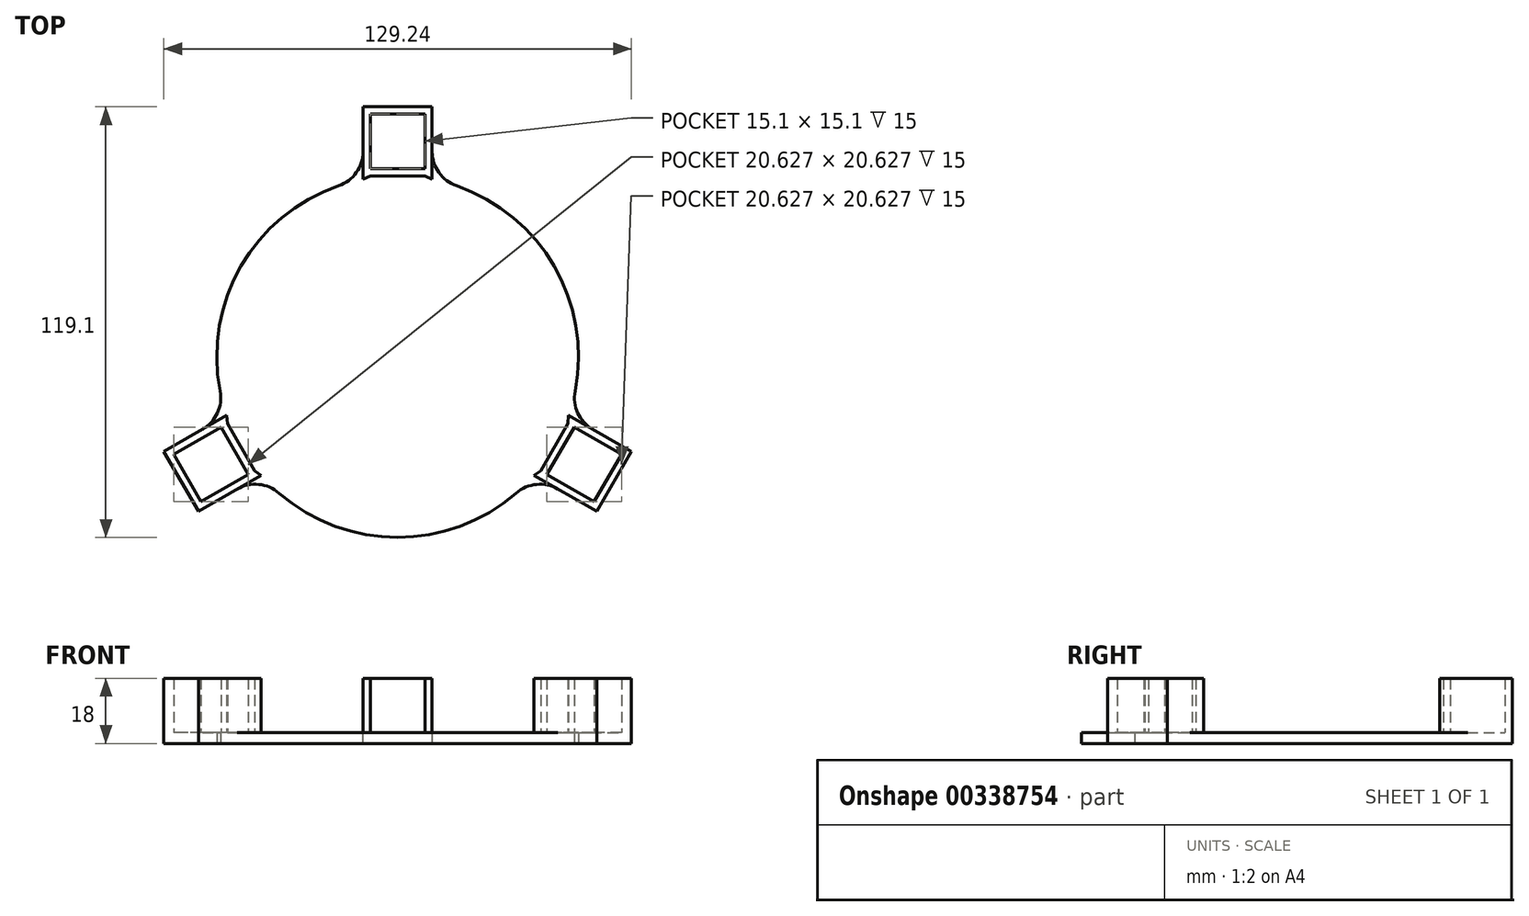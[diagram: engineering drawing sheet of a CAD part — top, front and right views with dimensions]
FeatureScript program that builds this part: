
annotation { "Feature Type Name" : "Feature", "Feature Type Description" : "" }
export const myFeature = defineFeature(function(context is Context, id is Id, definition is map)
    precondition{}
    {
        {
            var Q0;
            Q0=qCreatedBy(makeId("Top.planeOp"),FACE);
            var sketch = newSketch(context, id + "F0", { "sketchPlane" : qUnion([Q0])});
            skCircle(sketch, "E0", {"center": v(0, 0) * mm, "radius": 50 * mm});
            skSolve(sketch);
        }
        {
            var Q0;
            Q0=makeQuery(id+"F0.imprint","IMPRINT",FACE,{"disambiguationData":[TD([[makeQuery(id+"F0.imprint","IMPRINT",EDGE,{"derivedFrom":sQuery(id+"F0.wireOp",EDGE,"E0")}),1.0]])]});
            extrude(context, id + "F1", {"entities" : qUnion([Q0]), "depth" : 3 * mm});
        }
        {
            var Q0;
            Q0=qCreatedBy(makeId("Top.planeOp"),FACE);
            var sketch = newSketch(context, id + "F2", { "sketchPlane" : qUnion([Q0])});
            skLineSegment(sketch, "E1", {"start": v(0, 0) * mm, "end": v(0, 59.55) * mm, "construction": true});
            skCircle(sketch, "E2.0", {"center": v(0, 0) * mm, "radius": 50 * mm});
            skPoint(sketch, "E3", {"position": v(0, 50) * mm});
            skLineSegment(sketch, "E4.bottom", {"start": v(7.55, 50) * mm, "end": v(-7.55, 50) * mm});
            skLineSegment(sketch, "E4.top", {"start": v(7.55, 69.1) * mm, "end": v(-7.55, 69.1) * mm});
            skLineSegment(sketch, "E4.left", {"start": v(7.55, 50) * mm, "end": v(7.55, 69.1) * mm});
            skLineSegment(sketch, "E4.right", {"start": v(-7.55, 50) * mm, "end": v(-7.55, 69.1) * mm});
            skPoint(sketch, "E4.middle", {"position": v(0, 59.55) * mm});
            skLineSegment(sketch, "E5", {"start": v(-7.55, 52) * mm, "end": v(7.55, 52) * mm});
            skLineSegment(sketch, "E6", {"start": v(-7.55, 67.1) * mm, "end": v(7.55, 67.1) * mm});
            skLineSegment(sketch, "E7.bottom", {"start": v(-7.55, 69.1) * mm, "end": v(-9.55, 69.1) * mm});
            skLineSegment(sketch, "E7.top", {"start": v(-7.55, 67.1) * mm, "end": v(-9.55, 67.1) * mm});
            skLineSegment(sketch, "E7.left", {"start": v(-7.55, 69.1) * mm, "end": v(-7.55, 67.1) * mm});
            skLineSegment(sketch, "E7.right", {"start": v(-9.55, 69.1) * mm, "end": v(-9.55, 67.1) * mm});
            skLineSegment(sketch, "E8.bottom", {"start": v(7.55, 69.1) * mm, "end": v(9.55, 69.1) * mm});
            skLineSegment(sketch, "E8.top", {"start": v(7.55, 67.1) * mm, "end": v(9.55, 67.1) * mm});
            skLineSegment(sketch, "E8.left", {"start": v(7.55, 69.1) * mm, "end": v(7.55, 67.1) * mm});
            skLineSegment(sketch, "E8.right", {"start": v(9.55, 69.1) * mm, "end": v(9.55, 67.1) * mm});
            skLineSegment(sketch, "E9", {"start": v(-7.55, 50) * mm, "end": v(-9.55, 49.08) * mm});
            skLineSegment(sketch, "E10", {"start": v(7.55, 50) * mm, "end": v(9.55, 49.08) * mm});
            skLineSegment(sketch, "E11", {"start": v(-9.55, 67.1) * mm, "end": v(-9.55, 49.08) * mm});
            skLineSegment(sketch, "E12", {"start": v(9.55, 67.1) * mm, "end": v(9.55, 49.08) * mm});
            skLineSegment(sketch, "E13.1.0", {"start": v(-53.34, -41.82) * mm, "end": v(-37.73, -32.81) * mm});
            skLineSegment(sketch, "E13.1.1", {"start": v(-62.89, -25.28) * mm, "end": v(-47.28, -16.27) * mm});
            skLineSegment(sketch, "E13.1.2", {"start": v(-54.34, -40.09) * mm, "end": v(-61.89, -27.01) * mm});
            skLineSegment(sketch, "E13.1.3", {"start": v(-41.26, -32.54) * mm, "end": v(-48.8, -19.46) * mm});
            skLineSegment(sketch, "E13.1.4", {"start": v(-39.53, -31.54) * mm, "end": v(-56.07, -41.09) * mm});
            skLineSegment(sketch, "E13.1.5", {"start": v(-47.08, -18.46) * mm, "end": v(-63.62, -28.01) * mm});
            skLineSegment(sketch, "E13.1.6", {"start": v(-63.62, -28.01) * mm, "end": v(-56.07, -41.09) * mm});
            skLineSegment(sketch, "E13.1.7", {"start": v(-47.08, -18.46) * mm, "end": v(-39.53, -31.54) * mm});
            skLineSegment(sketch, "E13.1.8", {"start": v(0, 0) * mm, "end": v(-51.57, -29.77) * mm, "construction": true});
            skPoint(sketch, "E13.1.9", {"position": v(-51.57, -29.77) * mm});
            skPoint(sketch, "E13.1.10", {"position": v(-43.3, -25) * mm});
            skLineSegment(sketch, "E13.1.11", {"start": v(-47.08, -18.46) * mm, "end": v(-47.28, -16.27) * mm});
            skLineSegment(sketch, "E13.1.12", {"start": v(-39.53, -31.54) * mm, "end": v(-37.73, -32.81) * mm});
            skLineSegment(sketch, "E13.1.13", {"start": v(-54.34, -40.09) * mm, "end": v(-53.34, -41.82) * mm});
            skLineSegment(sketch, "E13.1.14", {"start": v(-56.07, -41.09) * mm, "end": v(-55.07, -42.82) * mm});
            skLineSegment(sketch, "E13.1.15", {"start": v(-56.07, -41.09) * mm, "end": v(-54.34, -40.09) * mm});
            skLineSegment(sketch, "E13.1.16", {"start": v(-63.62, -28.01) * mm, "end": v(-64.62, -26.28) * mm});
            skLineSegment(sketch, "E13.1.17", {"start": v(-55.07, -42.82) * mm, "end": v(-53.34, -41.82) * mm});
            skLineSegment(sketch, "E13.1.18", {"start": v(-64.62, -26.28) * mm, "end": v(-62.89, -25.28) * mm});
            skLineSegment(sketch, "E13.1.19", {"start": v(-63.62, -28.01) * mm, "end": v(-61.89, -27.01) * mm});
            skLineSegment(sketch, "E13.1.20", {"start": v(-61.89, -27.01) * mm, "end": v(-62.89, -25.28) * mm});
            skLineSegment(sketch, "E13.2.0", {"start": v(62.89, -25.28) * mm, "end": v(47.28, -16.27) * mm});
            skLineSegment(sketch, "E13.2.1", {"start": v(53.34, -41.82) * mm, "end": v(37.73, -32.81) * mm});
            skLineSegment(sketch, "E13.2.2", {"start": v(61.89, -27.01) * mm, "end": v(54.34, -40.09) * mm});
            skLineSegment(sketch, "E13.2.3", {"start": v(48.8, -19.46) * mm, "end": v(41.26, -32.54) * mm});
            skLineSegment(sketch, "E13.2.4", {"start": v(47.08, -18.46) * mm, "end": v(63.62, -28.01) * mm});
            skLineSegment(sketch, "E13.2.5", {"start": v(39.53, -31.54) * mm, "end": v(56.07, -41.09) * mm});
            skLineSegment(sketch, "E13.2.6", {"start": v(56.07, -41.09) * mm, "end": v(63.62, -28.01) * mm});
            skLineSegment(sketch, "E13.2.7", {"start": v(39.53, -31.54) * mm, "end": v(47.08, -18.46) * mm});
            skLineSegment(sketch, "E13.2.8", {"start": v(0, 0) * mm, "end": v(51.57, -29.78) * mm, "construction": true});
            skPoint(sketch, "E13.2.9", {"position": v(51.57, -29.78) * mm});
            skPoint(sketch, "E13.2.10", {"position": v(43.3, -25) * mm});
            skLineSegment(sketch, "E13.2.11", {"start": v(39.53, -31.54) * mm, "end": v(37.73, -32.81) * mm});
            skLineSegment(sketch, "E13.2.12", {"start": v(47.08, -18.46) * mm, "end": v(47.28, -16.27) * mm});
            skLineSegment(sketch, "E13.2.13", {"start": v(61.89, -27.01) * mm, "end": v(62.89, -25.28) * mm});
            skLineSegment(sketch, "E13.2.14", {"start": v(63.62, -28.01) * mm, "end": v(64.62, -26.28) * mm});
            skLineSegment(sketch, "E13.2.15", {"start": v(63.62, -28.01) * mm, "end": v(61.89, -27.01) * mm});
            skLineSegment(sketch, "E13.2.16", {"start": v(56.07, -41.09) * mm, "end": v(55.07, -42.82) * mm});
            skLineSegment(sketch, "E13.2.17", {"start": v(64.62, -26.28) * mm, "end": v(62.89, -25.28) * mm});
            skLineSegment(sketch, "E13.2.18", {"start": v(55.07, -42.82) * mm, "end": v(53.34, -41.82) * mm});
            skLineSegment(sketch, "E13.2.19", {"start": v(56.07, -41.09) * mm, "end": v(54.34, -40.09) * mm});
            skLineSegment(sketch, "E13.2.20", {"start": v(54.34, -40.09) * mm, "end": v(53.34, -41.82) * mm});
            skSolve(sketch);
        }
        {
            var Q0;
            {var subQ2=sQuery(id+"F2.wireOp",EDGE,"E5");Q0=makeQuery(id+"F2.imprint","IMPRINT",FACE,{"disambiguationData":[TD([[makeQuery(id+"F2.imprint","IMPRINT",EDGE,{"derivedFrom":subQ2}),1.0]])]});}
            var Q1;
            {var subQ0=sQuery(id+"F2.wireOp",EDGE,"E9");Q1=makeQuery(id+"F2.imprint","IMPRINT",FACE,{"disambiguationData":[TD([[makeQuery(id+"F2.imprint","IMPRINT",EDGE,{"derivedFrom":subQ0}),1.0]])]});}
            var Q2;
            {var subQ0=sQuery(id+"F2.wireOp",EDGE,"E10");Q2=makeQuery(id+"F2.imprint","IMPRINT",FACE,{"disambiguationData":[TD([[makeQuery(id+"F2.imprint","IMPRINT",EDGE,{"derivedFrom":subQ0}),-1.0]])]});}
            var Q3;
            {var subQ0=sQuery(id+"F2.wireOp",EDGE,"E13.2.2");Q3=makeQuery(id+"F2.imprint","IMPRINT",FACE,{"disambiguationData":[TD([[makeQuery(id+"F2.imprint","IMPRINT",EDGE,{"derivedFrom":subQ0}),-1.0]])]});}
            var Q4;
            {var subQ0=sQuery(id+"F2.wireOp",EDGE,"E13.2.12");Q4=makeQuery(id+"F2.imprint","IMPRINT",FACE,{"disambiguationData":[TD([[makeQuery(id+"F2.imprint","IMPRINT",EDGE,{"derivedFrom":subQ0}),1.0]])]});}
            var Q5;
            {var subQ0=sQuery(id+"F2.wireOp",EDGE,"E13.2.11");Q5=makeQuery(id+"F2.imprint","IMPRINT",FACE,{"disambiguationData":[TD([[makeQuery(id+"F2.imprint","IMPRINT",EDGE,{"derivedFrom":subQ0}),-1.0]])]});}
            var Q6;
            {var subQ0=sQuery(id+"F2.wireOp",EDGE,"E13.1.11");Q6=makeQuery(id+"F2.imprint","IMPRINT",FACE,{"disambiguationData":[TD([[makeQuery(id+"F2.imprint","IMPRINT",EDGE,{"derivedFrom":subQ0}),-1.0]])]});}
            var Q7;
            {var subQ0=sQuery(id+"F2.wireOp",EDGE,"E13.1.12");Q7=makeQuery(id+"F2.imprint","IMPRINT",FACE,{"disambiguationData":[TD([[makeQuery(id+"F2.imprint","IMPRINT",EDGE,{"derivedFrom":subQ0}),1.0]])]});}
            var Q8;
            {var subQ0=sQuery(id+"F2.wireOp",EDGE,"E13.1.2");Q8=makeQuery(id+"F2.imprint","IMPRINT",FACE,{"disambiguationData":[TD([[makeQuery(id+"F2.imprint","IMPRINT",EDGE,{"derivedFrom":subQ0}),-1.0]])]});}
            extrude(context, id + "F3", {"entities" : qUnion([Q0, Q1, Q2, Q3, Q4, Q5, Q6, Q7, Q8]), "operationType" : NewBodyOperationType.ADD, "depth" : 3 * mm});
        }
        {
            var Q0;
            Q0=makeQuery(id+"F2.imprint","IMPRINT",FACE,{"disambiguationData":[TD([[makeQuery(id+"F2.imprint","IMPRINT",EDGE,{"derivedFrom":sQuery(id+"F2.wireOp",EDGE,"E13.1.1")}),-1.0]])]});
            var Q1;
            {var subQ1=sQuery(id+"F2.wireOp",EDGE,"E13.1.3");Q1=makeQuery(id+"F2.imprint","IMPRINT",FACE,{"disambiguationData":[TD([[makeQuery(id+"F2.imprint","IMPRINT",EDGE,{"derivedFrom":subQ1}),-1.0]])]});}
            var Q2;
            Q2=makeQuery(id+"F2.imprint","IMPRINT",FACE,{"disambiguationData":[TD([[makeQuery(id+"F2.imprint","IMPRINT",EDGE,{"derivedFrom":sQuery(id+"F2.wireOp",EDGE,"E13.1.0")}),1.0]])]});
            var Q3;
            Q3=makeQuery(id+"F2.imprint","IMPRINT",FACE,{"disambiguationData":[TD([[makeQuery(id+"F2.imprint","IMPRINT",EDGE,{"derivedFrom":sQuery(id+"F2.wireOp",EDGE,"E13.1.2")}),1.0]])]});
            var Q4;
            Q4=makeQuery(id+"F2.imprint","IMPRINT",FACE,{"disambiguationData":[TD([[makeQuery(id+"F2.imprint","IMPRINT",EDGE,{"derivedFrom":sQuery(id+"F2.wireOp",EDGE,"E13.1.16")}),-1.0]])]});
            var Q5;
            Q5=makeQuery(id+"F2.imprint","IMPRINT",FACE,{"disambiguationData":[TD([[makeQuery(id+"F2.imprint","IMPRINT",EDGE,{"derivedFrom":sQuery(id+"F2.wireOp",EDGE,"E13.1.13")}),-1.0]])]});
            var Q6;
            {var subQ1=sQuery(id+"F2.wireOp",EDGE,"E13.2.3");Q6=makeQuery(id+"F2.imprint","IMPRINT",FACE,{"disambiguationData":[TD([[makeQuery(id+"F2.imprint","IMPRINT",EDGE,{"derivedFrom":subQ1}),-1.0]])]});}
            var Q7;
            Q7=makeQuery(id+"F2.imprint","IMPRINT",FACE,{"disambiguationData":[TD([[makeQuery(id+"F2.imprint","IMPRINT",EDGE,{"derivedFrom":sQuery(id+"F2.wireOp",EDGE,"E13.2.0")}),1.0]])]});
            var Q8;
            Q8=makeQuery(id+"F2.imprint","IMPRINT",FACE,{"disambiguationData":[TD([[makeQuery(id+"F2.imprint","IMPRINT",EDGE,{"derivedFrom":sQuery(id+"F2.wireOp",EDGE,"E13.2.13")}),-1.0]])]});
            var Q9;
            Q9=makeQuery(id+"F2.imprint","IMPRINT",FACE,{"disambiguationData":[TD([[makeQuery(id+"F2.imprint","IMPRINT",EDGE,{"derivedFrom":sQuery(id+"F2.wireOp",EDGE,"E13.2.2")}),1.0]])]});
            var Q10;
            Q10=makeQuery(id+"F2.imprint","IMPRINT",FACE,{"disambiguationData":[TD([[makeQuery(id+"F2.imprint","IMPRINT",EDGE,{"derivedFrom":sQuery(id+"F2.wireOp",EDGE,"E13.2.16")}),-1.0]])]});
            var Q11;
            Q11=makeQuery(id+"F2.imprint","IMPRINT",FACE,{"disambiguationData":[TD([[makeQuery(id+"F2.imprint","IMPRINT",EDGE,{"derivedFrom":sQuery(id+"F2.wireOp",EDGE,"E13.2.1")}),-1.0]])]});
            var Q12;
            Q12=makeQuery(id+"F2.imprint","IMPRINT",FACE,{"disambiguationData":[TD([[makeQuery(id+"F2.imprint","IMPRINT",EDGE,{"derivedFrom":sQuery(id+"F2.wireOp",EDGE,"E4.top")}),1.0]])]});
            var Q13;
            Q13=makeQuery(id+"F2.imprint","IMPRINT",FACE,{"disambiguationData":[TD([[makeQuery(id+"F2.imprint","IMPRINT",EDGE,{"derivedFrom":sQuery(id+"F2.wireOp",EDGE,"E7.bottom")}),1.0]])]});
            var Q14;
            Q14=makeQuery(id+"F2.imprint","IMPRINT",FACE,{"disambiguationData":[TD([[makeQuery(id+"F2.imprint","IMPRINT",EDGE,{"derivedFrom":sQuery(id+"F2.wireOp",EDGE,"E8.bottom")}),-1.0]])]});
            var Q15;
            {var subQ0=sQuery(id+"F2.wireOp",EDGE,"E8.top");Q15=makeQuery(id+"F2.imprint","IMPRINT",FACE,{"disambiguationData":[TD([[makeQuery(id+"F2.imprint","IMPRINT",EDGE,{"derivedFrom":subQ0}),-1.0]])]});}
            var Q16;
            {var subQ1=sQuery(id+"F2.wireOp",EDGE,"E7.top");Q16=makeQuery(id+"F2.imprint","IMPRINT",FACE,{"disambiguationData":[TD([[makeQuery(id+"F2.imprint","IMPRINT",EDGE,{"derivedFrom":subQ1}),1.0]])]});}
            var Q17;
            {var subQ3=sQuery(id+"F2.wireOp",EDGE,"E5");Q17=makeQuery(id+"F2.imprint","IMPRINT",FACE,{"disambiguationData":[TD([[makeQuery(id+"F2.imprint","IMPRINT",EDGE,{"derivedFrom":subQ3}),-1.0]])]});}
            extrude(context, id + "F4", {"entities" : qUnion([Q0, Q1, Q2, Q3, Q4, Q5, Q6, Q7, Q8, Q9, Q10, Q11, Q12, Q13, Q14, Q15, Q16, Q17]), "operationType" : NewBodyOperationType.ADD, "depth" : 18 * mm});
        }
        {
            var Q0;
            {var subQ0=sQuery(id+"F2.wireOp",EDGE,"E11");var subQ1=sQuery(id+"F2.wireOp",EDGE,"E9");var subQ2=sQuery(id+"F2.wireOp",EDGE,"E2.0");Q0=makeQuery(id+"F4.boolean.opBoolean","MERGE",EDGE,{"derivedFrom":[makeQuery(id+"F3.opExtrude","SWEPT_EDGE",EDGE,{"disambiguationData":[OSD([subQ2,subQ1,subQ0])]}),makeQuery(id+"F4.opExtrude","SWEPT_EDGE",EDGE,{"disambiguationData":[OSD([subQ2,subQ1,subQ0])]})]});}
            var Q1;
            {var subQ0=sQuery(id+"F2.wireOp",EDGE,"E12");var subQ1=sQuery(id+"F2.wireOp",EDGE,"E10");var subQ2=sQuery(id+"F2.wireOp",EDGE,"E2.0");Q1=makeQuery(id+"F4.boolean.opBoolean","MERGE",EDGE,{"derivedFrom":[makeQuery(id+"F3.opExtrude","SWEPT_EDGE",EDGE,{"disambiguationData":[OSD([subQ2,subQ1,subQ0])]}),makeQuery(id+"F4.opExtrude","SWEPT_EDGE",EDGE,{"disambiguationData":[OSD([subQ2,subQ1,subQ0])]})]});}
            var Q2;
            {var subQ0=sQuery(id+"F2.wireOp",EDGE,"E13.1.11");var subQ1=sQuery(id+"F2.wireOp",EDGE,"E13.1.1");var subQ2=sQuery(id+"F2.wireOp",EDGE,"E2.0");Q2=makeQuery(id+"F4.boolean.opBoolean","MERGE",EDGE,{"derivedFrom":[makeQuery(id+"F3.opExtrude","SWEPT_EDGE",EDGE,{"disambiguationData":[OSD([subQ2,subQ1,subQ0])]}),makeQuery(id+"F4.opExtrude","SWEPT_EDGE",EDGE,{"disambiguationData":[OSD([subQ2,subQ1,subQ0])]})]});}
            var Q3;
            {var subQ0=sQuery(id+"F2.wireOp",EDGE,"E13.1.12");var subQ1=sQuery(id+"F2.wireOp",EDGE,"E13.1.0");var subQ2=sQuery(id+"F2.wireOp",EDGE,"E2.0");Q3=makeQuery(id+"F4.boolean.opBoolean","MERGE",EDGE,{"derivedFrom":[makeQuery(id+"F3.opExtrude","SWEPT_EDGE",EDGE,{"disambiguationData":[OSD([subQ2,subQ1,subQ0])]}),makeQuery(id+"F4.opExtrude","SWEPT_EDGE",EDGE,{"disambiguationData":[OSD([subQ2,subQ1,subQ0])]})]});}
            var Q4;
            {var subQ0=sQuery(id+"F2.wireOp",EDGE,"E13.2.11");var subQ1=sQuery(id+"F2.wireOp",EDGE,"E13.2.1");var subQ2=sQuery(id+"F2.wireOp",EDGE,"E2.0");Q4=makeQuery(id+"F4.boolean.opBoolean","MERGE",EDGE,{"derivedFrom":[makeQuery(id+"F3.opExtrude","SWEPT_EDGE",EDGE,{"disambiguationData":[OSD([subQ2,subQ1,subQ0])]}),makeQuery(id+"F4.opExtrude","SWEPT_EDGE",EDGE,{"disambiguationData":[OSD([subQ2,subQ1,subQ0])]})]});}
            var Q5;
            {var subQ0=sQuery(id+"F2.wireOp",EDGE,"E13.2.12");var subQ1=sQuery(id+"F2.wireOp",EDGE,"E13.2.0");var subQ2=sQuery(id+"F2.wireOp",EDGE,"E2.0");Q5=makeQuery(id+"F4.boolean.opBoolean","MERGE",EDGE,{"derivedFrom":[makeQuery(id+"F3.opExtrude","SWEPT_EDGE",EDGE,{"disambiguationData":[OSD([subQ2,subQ1,subQ0])]}),makeQuery(id+"F4.opExtrude","SWEPT_EDGE",EDGE,{"disambiguationData":[OSD([subQ2,subQ1,subQ0])]})]});}
            fillet(context, id + "F5", {"entities" : qUnion([Q0, Q1, Q2, Q3, Q4, Q5]), "radius" : 10 * mm, "tangentPropagation" : true, "allowEdgeOverflow" : false});
        }
    });
